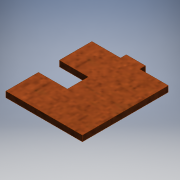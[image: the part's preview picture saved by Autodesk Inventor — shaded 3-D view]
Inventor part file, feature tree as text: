
AUTODESK INVENTOR PART (.ipt)
format: ipt  version: 2016 (Build 200138000, 138)  size: 146,432 bytes
history: native  units: mm
features: extrude x3, sketch x3, projected_geometry x2, other x1
ambient origin geometry x8: Origin, YZ Plane, XZ Plane, XY Plane, X Axis, Y Axis, Z Axis, Center Point
bodies: Body1 (feature_tree)
feature tree (9):
  other  "Sólido1"
  extrude  "Extrusión1"  Depth=3.0mm TaperAngle=0.0deg
  extrude  "Extrusión2"  Depth=2.0mm
  extrude  "Extrusión3"  [1 undecoded]
  sketch  "Boceto1"  dims[d0=3.0mm d1=0.0mm d2=3.0mm d3=0.0mm]
  sketch  "Boceto2"  dims[d4=1.0mm d5=2.0mm]
  projected_geometry  "Contorno proyectado1"
  sketch  "Boceto3"  dims[d6=3.0mm d7=0.0mm]
  projected_geometry  "Contorno proyectado2"
note: 1 required parameter value undecoded (feature->parameter linkage not recoverable at this tier; creation-order binding heuristic only, values carry confidence <= 0.55)
